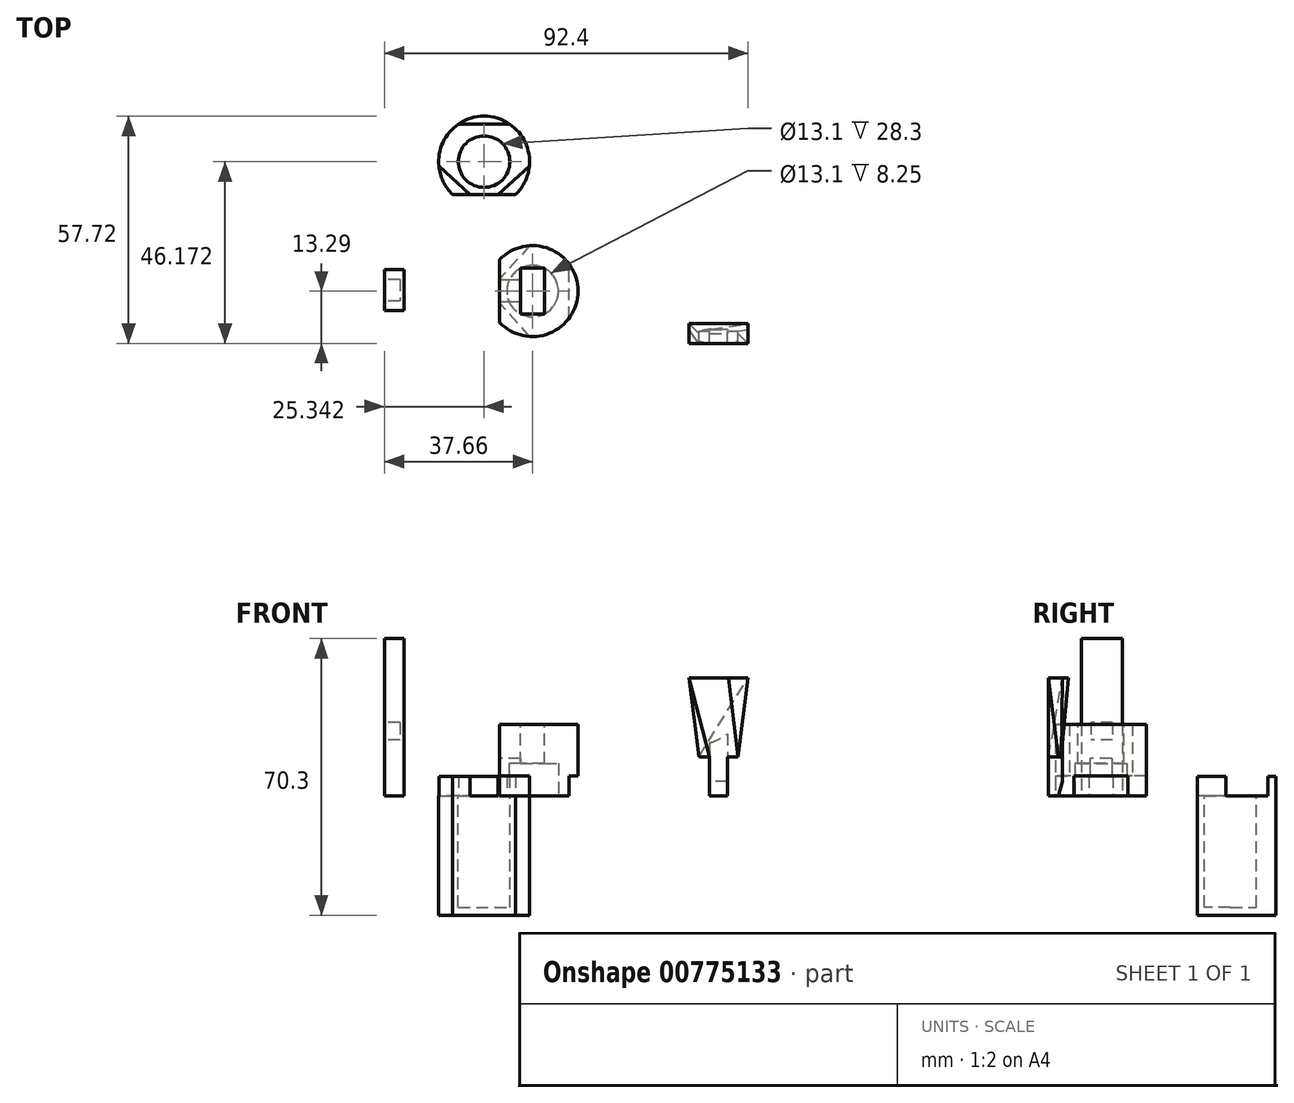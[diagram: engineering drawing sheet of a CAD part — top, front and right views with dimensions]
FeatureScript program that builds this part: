
annotation { "Feature Type Name" : "Feature", "Feature Type Description" : "" }
export const myFeature = defineFeature(function(context is Context, id is Id, definition is map)
    precondition{}
    {
        {
            var Q0;
            Q0=qCreatedBy(makeId("Top.planeOp"),FACE);
            var sketch = newSketch(context, id + "F0", { "sketchPlane" : qUnion([Q0])});
            skCircle(sketch, "E0", {"center": v(0, 0) * mm, "radius": 6.55 * mm});
            skCircle(sketch, "E1", {"center": v(0, 0) * mm, "radius": 11.55 * mm});
            skSolve(sketch);
        }
        {
            var Q0;
            Q0=makeQuery(id+"F0.imprint","IMPRINT",FACE,{"disambiguationData":[TD([[makeQuery(id+"F0.imprint","IMPRINT",EDGE,{"derivedFrom":sQuery(id+"F0.wireOp",EDGE,"E0")}),-1.0]])]});
            extrude(context, id + "F1", {"entities" : qUnion([Q0]), "depth" : (36.5 / 2) * mm, "offsetDistance" : 25 * mm});
        }
        {
            var Q0;
            Q0=makeQuery(id+"F1.opExtrude","CAP_FACE",FACE,{"disambiguationData":[OSD([sQuery(id+"F0.wireOp",EDGE,"E0"),sQuery(id+"F0.wireOp",EDGE,"E1")])],"isStart":false});
            var sketch = newSketch(context, id + "F2", { "sketchPlane" : qUnion([Q0])});
            skLineSegment(sketch, "E2", {"start": v(-3.05, 5.8) * mm, "end": v(-3.05, -5.8) * mm});
            skLineSegment(sketch, "E3", {"start": v(3.05, 5.8) * mm, "end": v(3.05, -5.8) * mm});
            skSolve(sketch);
        }
        {
            var Q0;
            {var subQ0=sQuery(id+"F2.wireOp",EDGE,"E3");Q0=makeQuery(id+"F2.imprint","IMPRINT",FACE,{"disambiguationData":[TD([[makeQuery(id+"F2.imprint","IMPRINT",EDGE,{"derivedFrom":subQ0}),1.0]])]});}
            var Q1;
            {var subQ0=sQuery(id+"F2.wireOp",EDGE,"E2");Q1=makeQuery(id+"F2.imprint","IMPRINT",FACE,{"disambiguationData":[TD([[makeQuery(id+"F2.imprint","IMPRINT",EDGE,{"derivedFrom":subQ0}),-1.0]])]});}
            extrude(context, id + "F3", {"entities" : qUnion([Q0, Q1]), "operationType" : NewBodyOperationType.ADD, "oppositeDirection" : true, "depth" : 10 * mm, "offsetDistance" : 25 * mm});
        }
        {
            var Q0;
            Q0=qCreatedBy(makeId("Top.planeOp"),FACE);
            var sketch = newSketch(context, id + "F4", { "sketchPlane" : qUnion([Q0])});
            skCircle(sketch, "E4", {"center": v(-12.32, 32.88) * mm, "radius": 6.55 * mm});
            skCircle(sketch, "E5", {"center": v(-12.32, 32.88) * mm, "radius": 11.55 * mm});
            skSolve(sketch);
        }
        {
            var Q0;
            Q0=makeQuery(id+"F4.imprint","IMPRINT",FACE,{"disambiguationData":[TD([[makeQuery(id+"F4.imprint","IMPRINT",EDGE,{"derivedFrom":sQuery(id+"F4.wireOp",EDGE,"E4")}),-1.0]])]});
            extrude(context, id + "F5", {"entities" : qUnion([Q0]), "oppositeDirection" : true, "depth" : (36.6 / 2 + 12) * mm, "offsetDistance" : 25 * mm});
        }
        {
            var Q0;
            Q0=makeQuery(id+"F5.opExtrude","CAP_FACE",FACE,{"disambiguationData":[OSD([sQuery(id+"F4.wireOp",EDGE,"E4"),sQuery(id+"F4.wireOp",EDGE,"E5")])],"isStart":false});
            var sketch = newSketch(context, id + "F6", { "sketchPlane" : qUnion([Q0])});
            skCircle(sketch, "E6", {"center": v(-12.32, -32.88) * mm, "radius": 6.55 * mm});
            skSolve(sketch);
        }
        {
            var Q0;
            Q0=makeQuery(id+"F6.imprint","IMPRINT",FACE,{"disambiguationData":[TD([[makeQuery(id+"F6.imprint","IMPRINT",EDGE,{"derivedFrom":sQuery(id+"F6.wireOp",EDGE,"E6")}),-1.0]])]});
            extrude(context, id + "F7", {"entities" : qUnion([Q0]), "operationType" : NewBodyOperationType.ADD, "oppositeDirection" : true, "depth" : 2 * mm, "offsetDistance" : 25 * mm});
        }
        {
            var Q0;
            Q0=makeQuery(id+"F7.boolean.opBoolean","MERGE",FACE,{"derivedFrom":[makeQuery(id+"F5.opExtrude","CAP_FACE",FACE,{"disambiguationData":[OSD([sQuery(id+"F4.wireOp",EDGE,"E4"),sQuery(id+"F4.wireOp",EDGE,"E5")])],"isStart":false}),makeQuery(id+"F7.opExtrude","CAP_FACE",FACE,{"disambiguationData":[OSD([sQuery(id+"F6.wireOp",EDGE,"E6")])],"isStart":true})]});
            var sketch = newSketch(context, id + "F8", { "sketchPlane" : qUnion([Q0])});
            skLineSegment(sketch, "E7", {"start": v(-20.32, -24.55) * mm, "end": v(-4.32, -24.55) * mm});
            skSolve(sketch);
        }
        {
            var Q0;
            {var subQ0=sQuery(id+"F8.wireOp",EDGE,"E7");Q0=makeQuery(id+"F8.imprint","IMPRINT",FACE,{"disambiguationData":[TD([[makeQuery(id+"F8.imprint","IMPRINT",EDGE,{"derivedFrom":subQ0}),1.0]])]});}
            extrude(context, id + "F9", {"entities" : qUnion([Q0]), "operationType" : NewBodyOperationType.REMOVE, "oppositeDirection" : true, "depth" : 40 * mm, "offsetDistance" : 25 * mm});
        }
        {
            var Q0;
            Q0=makeQuery(id+"F1.opExtrude","CAP_FACE",FACE,{"disambiguationData":[OSD([sQuery(id+"F0.wireOp",EDGE,"E0"),sQuery(id+"F0.wireOp",EDGE,"E1")])],"isStart":true});
            var sketch = newSketch(context, id + "F10", { "sketchPlane" : qUnion([Q0])});
            skLineSegment(sketch, "E8", {"start": v(-8.33, -8) * mm, "end": v(-8.33, 8) * mm});
            skSolve(sketch);
        }
        {
            var Q0;
            {var subQ0=sQuery(id+"F10.wireOp",EDGE,"E8");Q0=makeQuery(id+"F10.imprint","IMPRINT",FACE,{"disambiguationData":[TD([[makeQuery(id+"F10.imprint","IMPRINT",EDGE,{"derivedFrom":subQ0}),1.0]])]});}
            extrude(context, id + "F11", {"entities" : qUnion([Q0]), "operationType" : NewBodyOperationType.REMOVE, "oppositeDirection" : true, "depth" : 25 * mm, "offsetDistance" : 25 * mm});
        }
        {
            var Q0;
            Q0=makeQuery(id+"F11.boolean.opBoolean","COPY",FACE,{"derivedFrom":makeQuery(id+"F11.opExtrude","SWEPT_FACE",FACE,{"disambiguationData":[OSD([sQuery(id+"F10.wireOp",EDGE,"E8")])]})});
            var sketch = newSketch(context, id + "F12", { "sketchPlane" : qUnion([Q0])});
            skLineSegment(sketch, "E9.bottom", {"start": v(-2.75, 9.5) * mm, "end": v(2.75, 9.5) * mm});
            skLineSegment(sketch, "E9.top", {"start": v(-2.75, 5) * mm, "end": v(2.75, 5) * mm});
            skLineSegment(sketch, "E9.left", {"start": v(-2.75, 9.5) * mm, "end": v(-2.75, 5) * mm});
            skLineSegment(sketch, "E9.right", {"start": v(2.75, 9.5) * mm, "end": v(2.75, 5) * mm});
            skLineSegment(sketch, "E10", {"start": v(-2.75, 7.25) * mm, "end": v(-8, 7.25) * mm});
            skLineSegment(sketch, "E11", {"start": v(2.75, 7.25) * mm, "end": v(8, 7.25) * mm});
            skSolve(sketch);
        }
        {
            var Q0;
            Q0 = qSketchRegion(id + "F12", true);
            extrude(context, id + "F13", {"entities" : qUnion([Q0]), "operationType" : NewBodyOperationType.REMOVE, "oppositeDirection" : true, "depth" : 10 * mm, "offsetDistance" : 25 * mm});
        }
        {
            var Q0;
            Q0=qCreatedBy(makeId("Top.planeOp"),FACE);
            var sketch = newSketch(context, id + "F14", { "sketchPlane" : qUnion([Q0])});
            skLineSegment(sketch, "E12.bottom", {"start": v(49.5, -13.29) * mm, "end": v(45, -13.29) * mm});
            skLineSegment(sketch, "E12.top", {"start": v(49.5, -9.79) * mm, "end": v(45, -9.79) * mm});
            skLineSegment(sketch, "E12.left", {"start": v(49.5, -13.29) * mm, "end": v(49.5, -9.79) * mm});
            skLineSegment(sketch, "E12.right", {"start": v(45, -13.29) * mm, "end": v(45, -9.79) * mm});
            skSolve(sketch);
        }
        {
            var Q0;
            Q0 = qSketchRegion(id + "F14", true);
            extrude(context, id + "F15", {"entities" : qUnion([Q0]), "depth" : 30 * mm, "offsetDistance" : 25 * mm});
        }
        {
            var Q0;
            {var subQ0=sQuery(id+"F0.wireOp",EDGE,"E0");Q0=makeQuery(id+"F3.boolean.opBoolean","MERGE",FACE,{"derivedFrom":[makeQuery(id+"F1.opExtrude","CAP_FACE",FACE,{"disambiguationData":[OSD([subQ0,sQuery(id+"F0.wireOp",EDGE,"E1")])],"isStart":false}),makeQuery(id+"F3.opExtrude","CAP_FACE",FACE,{"disambiguationData":[OSD([subQ0,sQuery(id+"F2.wireOp",EDGE,"E2")])],"isStart":true}),makeQuery(id+"F3.opExtrude","CAP_FACE",FACE,{"disambiguationData":[OSD([subQ0,sQuery(id+"F2.wireOp",EDGE,"E3")])],"isStart":true})]});}
            var sketch = newSketch(context, id + "F16", { "sketchPlane" : qUnion([Q0])});
            skLineSegment(sketch, "E13", {"start": v(-3.05, 5.8) * mm, "end": v(3.05, 5.8) * mm});
            skLineSegment(sketch, "E14", {"start": v(3.05, -5.8) * mm, "end": v(-3.05, -5.8) * mm});
            skSolve(sketch);
        }
        {
            var Q0;
            Q0=makeQuery(id+"F16.imprint","IMPRINT",FACE,{"disambiguationData":[TD([[makeQuery(id+"F16.imprint","IMPRINT",EDGE,{"derivedFrom":sQuery(id+"F16.wireOp",EDGE,"E13")}),1.0]])]});
            var Q1;
            Q1=makeQuery(id+"F16.imprint","IMPRINT",FACE,{"disambiguationData":[TD([[makeQuery(id+"F16.imprint","IMPRINT",EDGE,{"derivedFrom":sQuery(id+"F16.wireOp",EDGE,"E14")}),1.0]])]});
            extrude(context, id + "F17", {"entities" : qUnion([Q0, Q1]), "operationType" : NewBodyOperationType.ADD, "oppositeDirection" : true, "depth" : 10 * mm, "offsetDistance" : 25 * mm});
        }
        {
            var Q0;
            Q0=qCreatedBy(makeId("Top.planeOp"),FACE);
            var sketch = newSketch(context, id + "F18", { "sketchPlane" : qUnion([Q0])});
            skLineSegment(sketch, "E15.bottom", {"start": v(-37.66, 5.43) * mm, "end": v(-32.66, 5.43) * mm});
            skLineSegment(sketch, "E15.top", {"start": v(-37.66, -4.97) * mm, "end": v(-32.66, -4.97) * mm});
            skLineSegment(sketch, "E15.left", {"start": v(-37.66, 5.43) * mm, "end": v(-37.66, -4.97) * mm});
            skLineSegment(sketch, "E15.right", {"start": v(-32.66, 5.43) * mm, "end": v(-32.66, -4.97) * mm});
            skSolve(sketch);
        }
        {
            var Q0;
            Q0 = qSketchRegion(id + "F18", true);
            extrude(context, id + "F19", {"entities" : qUnion([Q0]), "depth" : 40 * mm, "offsetDistance" : 25 * mm});
        }
        {
            var Q0;
            Q0=makeQuery(id+"F19.opExtrude","SWEPT_FACE",FACE,{"disambiguationData":[OSD([sQuery(id+"F18.wireOp",EDGE,"E15.left")])]});
            var sketch = newSketch(context, id + "F20", { "sketchPlane" : qUnion([Q0])});
            skLineSegment(sketch, "E16.bottom", {"start": v(-2.98, 18.7) * mm, "end": v(2.52, 18.7) * mm});
            skLineSegment(sketch, "E16.top", {"start": v(-2.98, 14.2) * mm, "end": v(2.52, 14.2) * mm});
            skLineSegment(sketch, "E16.left", {"start": v(-2.98, 18.7) * mm, "end": v(-2.98, 14.2) * mm});
            skLineSegment(sketch, "E16.right", {"start": v(2.52, 18.7) * mm, "end": v(2.52, 14.2) * mm});
            skLineSegment(sketch, "E17", {"start": v(-2.98, 16.45) * mm, "end": v(-5.43, 16.45) * mm});
            skLineSegment(sketch, "E18", {"start": v(2.52, 16.45) * mm, "end": v(4.97, 16.45) * mm});
            skSolve(sketch);
        }
        {
            var Q0;
            Q0 = qSketchRegion(id + "F20", true);
            extrude(context, id + "F21", {"entities" : qUnion([Q0]), "operationType" : NewBodyOperationType.REMOVE, "oppositeDirection" : true, "depth" : 4 * mm, "offsetDistance" : 25 * mm});
        }
        {
            var Q0;
            Q0=makeQuery(id+"F5.opExtrude","CAP_FACE",FACE,{"disambiguationData":[OSD([sQuery(id+"F4.wireOp",EDGE,"E4"),sQuery(id+"F4.wireOp",EDGE,"E5")])],"isStart":true});
            var sketch = newSketch(context, id + "F22", { "sketchPlane" : qUnion([Q0])});
            skLineSegment(sketch, "E19", {"start": v(-23.81, 31.73) * mm, "end": v(-15.83, 24.55) * mm});
            skLineSegment(sketch, "E20", {"start": v(-20.32, 24.55) * mm, "end": v(-18.31, 26.78) * mm});
            skLineSegment(sketch, "E21", {"start": v(-8.8, 24.55) * mm, "end": v(-0.83, 31.73) * mm});
            skLineSegment(sketch, "E22", {"start": v(-4.32, 24.55) * mm, "end": v(-6.33, 26.78) * mm});
            skLineSegment(sketch, "E23", {"start": v(-18.81, 42.43) * mm, "end": v(-5.82, 42.43) * mm});
            skLineSegment(sketch, "E24", {"start": v(-12.32, 44.43) * mm, "end": v(-12.32, 42.43) * mm});
            skSolve(sketch);
        }
        {
            var Q0;
            {var subQ3=sQuery(id+"F22.wireOp",EDGE,"E24");Q0=makeQuery(id+"F22.imprint","IMPRINT",FACE,{"disambiguationData":[TD([[makeQuery(id+"F22.imprint","IMPRINT",EDGE,{"derivedFrom":subQ3}),-1.0]])]});}
            var Q1;
            {var subQ3=sQuery(id+"F22.wireOp",EDGE,"E24");Q1=makeQuery(id+"F22.imprint","IMPRINT",FACE,{"disambiguationData":[TD([[makeQuery(id+"F22.imprint","IMPRINT",EDGE,{"derivedFrom":subQ3}),1.0]])]});}
            var Q2;
            {var subQ4=sQuery(id+"F22.wireOp",EDGE,"E22");Q2=makeQuery(id+"F22.imprint","IMPRINT",FACE,{"disambiguationData":[TD([[makeQuery(id+"F22.imprint","IMPRINT",EDGE,{"derivedFrom":subQ4}),-1.0]])]});}
            var Q3;
            {var subQ4=sQuery(id+"F22.wireOp",EDGE,"E22");Q3=makeQuery(id+"F22.imprint","IMPRINT",FACE,{"disambiguationData":[TD([[makeQuery(id+"F22.imprint","IMPRINT",EDGE,{"derivedFrom":subQ4}),1.0]])]});}
            var Q4;
            {var subQ4=sQuery(id+"F22.wireOp",EDGE,"E20");Q4=makeQuery(id+"F22.imprint","IMPRINT",FACE,{"disambiguationData":[TD([[makeQuery(id+"F22.imprint","IMPRINT",EDGE,{"derivedFrom":subQ4}),-1.0]])]});}
            var Q5;
            {var subQ4=sQuery(id+"F22.wireOp",EDGE,"E20");Q5=makeQuery(id+"F22.imprint","IMPRINT",FACE,{"disambiguationData":[TD([[makeQuery(id+"F22.imprint","IMPRINT",EDGE,{"derivedFrom":subQ4}),1.0]])]});}
            extrude(context, id + "F23", {"entities" : qUnion([Q0, Q1, Q2, Q3, Q4, Q5]), "operationType" : NewBodyOperationType.ADD, "depth" : 5 * mm, "offsetDistance" : 25 * mm});
        }
        {
            var Q0;
            Q0=makeQuery(id+"F1.opExtrude","CAP_FACE",FACE,{"disambiguationData":[OSD([sQuery(id+"F0.wireOp",EDGE,"E0"),sQuery(id+"F0.wireOp",EDGE,"E1")])],"isStart":true});
            var sketch = newSketch(context, id + "F24", { "sketchPlane" : qUnion([Q0])});
            skLineSegment(sketch, "E25", {"start": v(-0.71, 11.53) * mm, "end": v(-8.33, 3.07) * mm});
            skLineSegment(sketch, "E26", {"start": v(-0.71, -11.53) * mm, "end": v(-8.33, -3.07) * mm});
            skLineSegment(sketch, "E27", {"start": v(9.25, 6.92) * mm, "end": v(9.25, -6.92) * mm});
            skLineSegment(sketch, "E28", {"start": v(11.55, 0) * mm, "end": v(9.25, 0) * mm});
            skLineSegment(sketch, "E29", {"start": v(-8.33, -8) * mm, "end": v(-5.88, -5.8) * mm});
            skLineSegment(sketch, "E30", {"start": v(-8.33, 8) * mm, "end": v(-5.88, 5.8) * mm});
            skSolve(sketch);
        }
        {
            var Q0;
            {var subQ4=sQuery(id+"F24.wireOp",EDGE,"E29");Q0=makeQuery(id+"F24.imprint","IMPRINT",FACE,{"disambiguationData":[TD([[makeQuery(id+"F24.imprint","IMPRINT",EDGE,{"derivedFrom":subQ4}),1.0]])]});}
            var Q1;
            {var subQ5=sQuery(id+"F24.wireOp",EDGE,"E29");Q1=makeQuery(id+"F24.imprint","IMPRINT",FACE,{"disambiguationData":[TD([[makeQuery(id+"F24.imprint","IMPRINT",EDGE,{"derivedFrom":subQ5}),-1.0]])]});}
            var Q2;
            {var subQ5=sQuery(id+"F24.wireOp",EDGE,"E30");Q2=makeQuery(id+"F24.imprint","IMPRINT",FACE,{"disambiguationData":[TD([[makeQuery(id+"F24.imprint","IMPRINT",EDGE,{"derivedFrom":subQ5}),1.0]])]});}
            var Q3;
            {var subQ4=sQuery(id+"F24.wireOp",EDGE,"E30");Q3=makeQuery(id+"F24.imprint","IMPRINT",FACE,{"disambiguationData":[TD([[makeQuery(id+"F24.imprint","IMPRINT",EDGE,{"derivedFrom":subQ4}),-1.0]])]});}
            var Q4;
            {var subQ3=sQuery(id+"F24.wireOp",EDGE,"E28");Q4=makeQuery(id+"F24.imprint","IMPRINT",FACE,{"disambiguationData":[TD([[makeQuery(id+"F24.imprint","IMPRINT",EDGE,{"derivedFrom":subQ3}),1.0]])]});}
            var Q5;
            {var subQ3=sQuery(id+"F24.wireOp",EDGE,"E28");Q5=makeQuery(id+"F24.imprint","IMPRINT",FACE,{"disambiguationData":[TD([[makeQuery(id+"F24.imprint","IMPRINT",EDGE,{"derivedFrom":subQ3}),-1.0]])]});}
            extrude(context, id + "F25", {"entities" : qUnion([Q0, Q1, Q2, Q3, Q4, Q5]), "operationType" : NewBodyOperationType.REMOVE, "oppositeDirection" : true, "depth" : 5.1 * mm, "offsetDistance" : 25 * mm});
        }
        {
            var Q0;
            Q0=makeQuery(id+"F15.opExtrude","CAP_EDGE",EDGE,{"disambiguationData":[OSD([sQuery(id+"F14.wireOp",EDGE,"E12.top")])],"isStart":true});
            chamfer(context, id + "F26", {"entities" : qUnion([Q0]), "chamferType" : ChamferType.TWO_OFFSETS, "width1" : 3.7 * mm, "oppositeDirection" : false, "width2" : 1 * mm});
        }
        {
            var Q0;
            Q0=makeQuery(id+"F15.opExtrude","CAP_FACE",FACE,{"disambiguationData":[OSD([sQuery(id+"F14.wireOp",EDGE,"E12.bottom"),sQuery(id+"F14.wireOp",EDGE,"E12.top"),sQuery(id+"F14.wireOp",EDGE,"E12.left"),sQuery(id+"F14.wireOp",EDGE,"E12.right")])],"isStart":false});
            var sketch = newSketch(context, id + "F27", { "sketchPlane" : qUnion([Q0])});
            skLineSegment(sketch, "E31.bottom", {"start": v(39.74, -13.29) * mm, "end": v(54.74, -13.29) * mm});
            skLineSegment(sketch, "E31.top", {"start": v(39.74, -8.29) * mm, "end": v(54.74, -8.29) * mm});
            skLineSegment(sketch, "E31.left", {"start": v(39.74, -13.29) * mm, "end": v(39.74, -8.29) * mm});
            skLineSegment(sketch, "E31.right", {"start": v(54.74, -13.29) * mm, "end": v(54.74, -8.29) * mm});
            skLineSegment(sketch, "E32", {"start": v(39.74, -9.79) * mm, "end": v(45, -9.79) * mm});
            skLineSegment(sketch, "E33", {"start": v(49.5, -9.79) * mm, "end": v(54.74, -9.79) * mm});
            skSolve(sketch);
        }
        {
            var Q0;
            {var subQ4=sQuery(id+"F27.wireOp",EDGE,"E32");Q0=makeQuery(id+"F27.imprint","IMPRINT",FACE,{"disambiguationData":[TD([[makeQuery(id+"F27.imprint","IMPRINT",EDGE,{"derivedFrom":subQ4}),-1.0]])]});}
            cPlane(context, id + "F28", {"entities" : qUnion([Q0]), "cplaneType" : CPlaneType.OFFSET, "offset" : 20 * mm, "oppositeDirection" : true, "width" : 150 * mm, "height" : 150 * mm});
        }
        {
            var Q0;
            Q0=qCreatedBy(id+"F28.planeOp",FACE);
            var sketch = newSketch(context, id + "F29", { "sketchPlane" : qUnion([Q0])});
            skLineSegment(sketch, "E34.0.0", {"start": v(45, -13.29) * mm, "end": v(45, -10.79) * mm});
            skLineSegment(sketch, "E34.0.1", {"start": v(45, -10.79) * mm, "end": v(49.5, -10.79) * mm});
            skLineSegment(sketch, "E34.0.2", {"start": v(49.5, -10.79) * mm, "end": v(49.5, -13.29) * mm});
            skLineSegment(sketch, "E34.0.3", {"start": v(49.5, -13.29) * mm, "end": v(45, -13.29) * mm});
            skLineSegment(sketch, "E35.bottom", {"start": v(42.24, -13.29) * mm, "end": v(52.24, -13.29) * mm});
            skLineSegment(sketch, "E35.top", {"start": v(42.24, -10.09) * mm, "end": v(52.24, -10.09) * mm});
            skLineSegment(sketch, "E35.left", {"start": v(42.24, -13.29) * mm, "end": v(42.24, -10.09) * mm});
            skLineSegment(sketch, "E35.right", {"start": v(52.24, -13.29) * mm, "end": v(52.24, -10.09) * mm});
            skLineSegment(sketch, "E36", {"start": v(45, -10.79) * mm, "end": v(42.24, -10.79) * mm});
            skLineSegment(sketch, "E37", {"start": v(49.5, -10.79) * mm, "end": v(52.24, -10.79) * mm});
            skSolve(sketch);
        }
        {
            var Q1;
            Q1 = qSketchRegion(id + "F29", true);
            var Q2;
            Q2 = qSketchRegion(id + "F27", true);
            loft(context, id + "F30", {"operationType" : NewBodyOperationType.ADD, "sheetProfilesArray" : [{ "sheetProfileEntities" : qUnion([Q1]) }, { "sheetProfileEntities" : qUnion([Q2]) }]});
        }
    });
